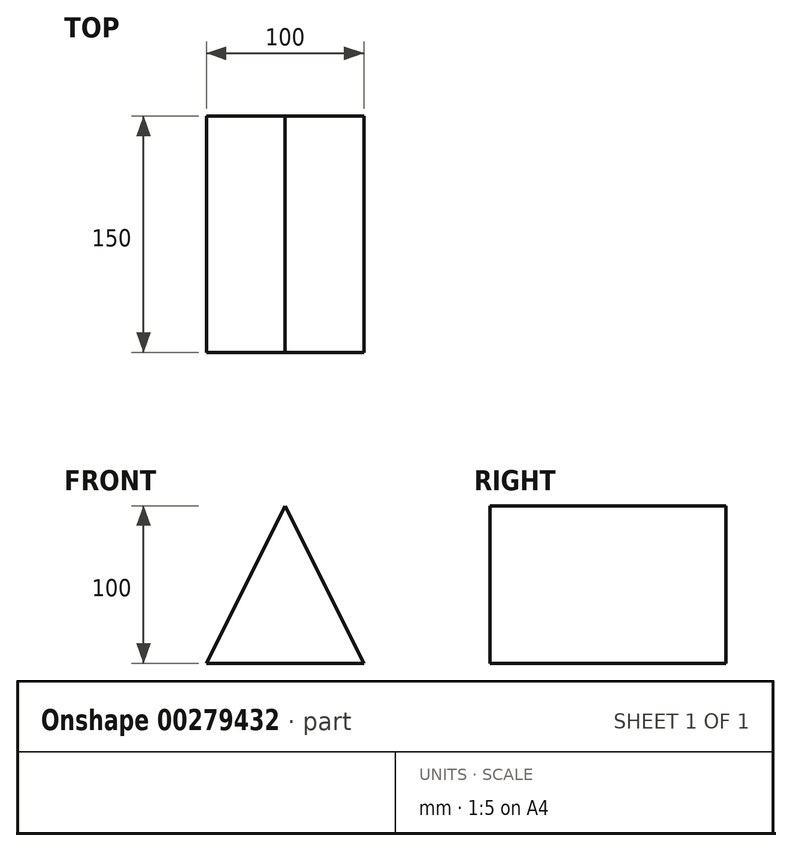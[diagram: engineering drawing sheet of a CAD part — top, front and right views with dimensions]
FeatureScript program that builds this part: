
annotation { "Feature Type Name" : "Feature", "Feature Type Description" : "" }
export const myFeature = defineFeature(function(context is Context, id is Id, definition is map)
    precondition{}
    {
        {
            var Q0;
            Q0=qCreatedBy(makeId("Front.planeOp"),FACE);
            var sketch = newSketch(context, id + "F0", { "sketchPlane" : qUnion([Q0])});
            skLineSegment(sketch, "E0.top", {"start": v(-50, -50) * mm, "end": v(50, -50) * mm});
            skLineSegment(sketch, "E1", {"start": v(-50, -50) * mm, "end": v(0, 50) * mm});
            skLineSegment(sketch, "E2", {"start": v(0, 50) * mm, "end": v(50, -50) * mm});
            skPoint(sketch, "E3.orphan", {"position": v(50, 50) * mm});
            skPoint(sketch, "E0.bottom.start.orphan", {"position": v(-50, 50) * mm});
            skSolve(sketch);
        }
        {
            var Q0;
            Q0=makeQuery(id+"F0.imprint","IMPRINT",FACE,{"disambiguationData":[TD([[makeQuery(id+"F0.imprint","IMPRINT",EDGE,{"derivedFrom":sQuery(id+"F0.wireOp",EDGE,"E0.top")}),1.0]])]});
            extrude(context, id + "F1", {"entities" : qUnion([Q0]), "depth" : 150 * mm});
        }
        {
            var Q0;
            Q0=makeQuery(id+"F1.opExtrude","CAP_FACE",FACE,{"disambiguationData":[OSD([sQuery(id+"F0.wireOp",EDGE,"E0.top"),sQuery(id+"F0.wireOp",EDGE,"E1"),sQuery(id+"F0.wireOp",EDGE,"E2")])],"isStart":false});
            var sketch = newSketch(context, id + "F2", { "sketchPlane" : qUnion([Q0])});
            skCircle(sketch, "E4", {"center": v(0, 0) * mm, "radius": 20.86 * mm});
            skArc(sketch, "E5", {"start": v(-20.93, -24.01) * mm, "mid": v(-27.94, -41.23) * mm, "end": v(-11, -33.58) * mm});
            skLineSegment(sketch, "E6", {"start": v(-21.07, -24.01) * mm, "end": v(-11, -24.01) * mm});
            skLineSegment(sketch, "E7", {"start": v(-11, -33.58) * mm, "end": v(-11, -24.01) * mm});
            skArc(sketch, "E8", {"start": v(10.98, -35.1) * mm, "mid": v(27.7, -39.78) * mm, "end": v(20.42, -24.01) * mm});
            skPoint(sketch, "E9.end.orphan", {"position": v(7.66, -24.01) * mm});
            skLineSegment(sketch, "E10", {"start": v(-20.93, -24.01) * mm, "end": v(-11, -24.01) * mm});
            skLineSegment(sketch, "E11", {"start": v(10.98, -35.1) * mm, "end": v(10.85, -33.58) * mm});
            skLineSegment(sketch, "E12", {"start": v(10.85, -33.58) * mm, "end": v(7.66, -24.01) * mm});
            skPoint(sketch, "E13.start.orphan", {"position": v(0, -26.68) * mm});
            skPoint(sketch, "E14.start.orphan", {"position": v(-21, -44.03) * mm});
            skLineSegment(sketch, "E15.trimOffspring", {"start": v(7.66, -24.01) * mm, "end": v(20.42, -24.01) * mm});
            skSolve(sketch);
        }
        {
            var Q0;
            Q0=makeQuery(id+"F2.imprint","IMPRINT",FACE,{"disambiguationData":[TD([[makeQuery(id+"F2.imprint","IMPRINT",EDGE,{"derivedFrom":sQuery(id+"F2.wireOp",EDGE,"E4")}),1.0]])]});
            extrude(context, id + "F3", {"entities" : qUnion([Q0]), "operationType" : NewBodyOperationType.REMOVE, "depth" : 25 * mm, "hasDraft" : true, "draftAngle" : 3 * degree});
        }
    });
